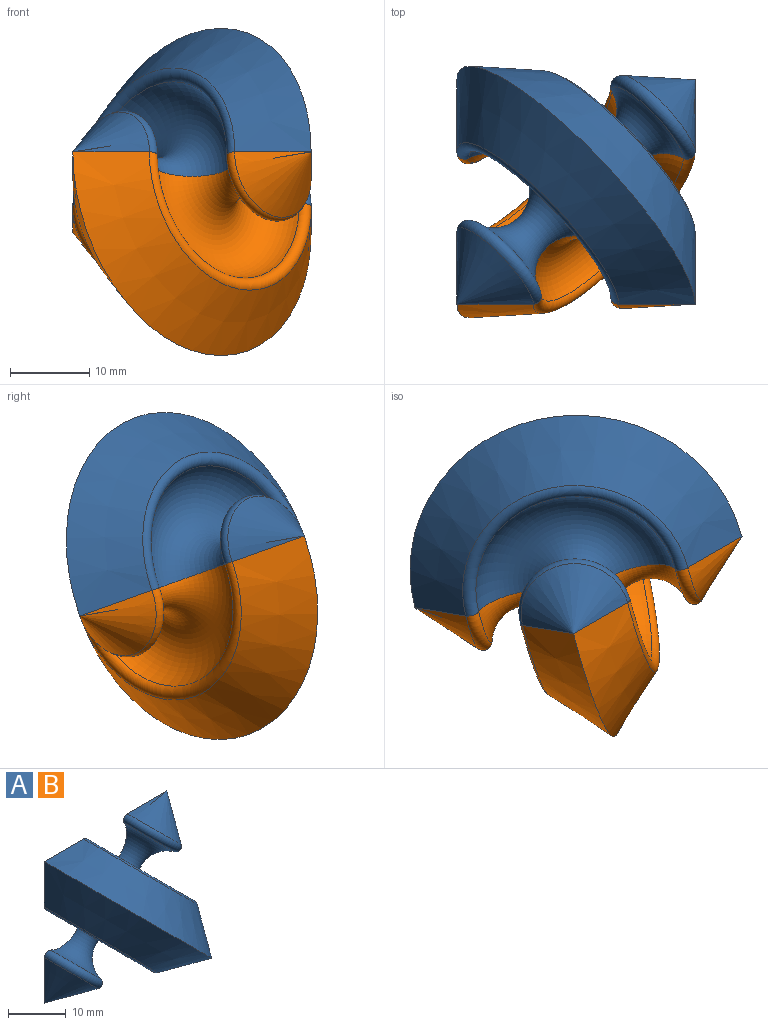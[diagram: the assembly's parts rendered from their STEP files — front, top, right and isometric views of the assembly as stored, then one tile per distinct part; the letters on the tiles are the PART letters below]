
ASSEMBLY  parts=2 mates=1
PART A: 11 faces, bbox 31.7x21.2x31.7 mm
  f0: torus R=7.78mm, axis (-0.71,0,-0.71), area 420.7mm2, adj f6,f7,f10
  f1: cone r=12.9mm half-angle=45deg, axis (-0.71,0,-0.71), area 538.8mm2, adj f2,f6,f7
  f2: cone r=21.21mm half-angle=45deg, axis (0.71,0,0.71), area 538.8mm2, adj f1,f6,f8
  f3: torus R=7.78mm, axis (-0.71,0,-0.71), area 420.7mm2, adj f6,f8,f9
  f4: cone r=8.31mm half-angle=45deg, axis (0.71,0,0.71), area 103mm2, adj f6,f9
  f5: cone r=0mm half-angle=45deg, axis (-0.71,0,-0.71), area 103mm2, adj f6,f10
  f6: plane 30x30mm, normal (0,1,0), area 580.2mm2, adj f0,f1,f2,f3,f4,f5,f7,f8
  f7: torus R=13.7mm, axis (0.71,0,0.71), area 88.1mm2, adj f0,f1,f6
  f8: torus R=13.7mm, axis (0.71,0,0.71), area 88.1mm2, adj f2,f3,f6
  f9: torus R=6.1mm, axis (0.71,0,0.71), area 45.1mm2, adj f3,f4,f6
  f10: torus R=6.1mm, axis (0.71,0,0.71), area 45.1mm2, adj f0,f5,f6
PART B: same geometry as A
PLACE A rot(axis=(-1,0,0),109.7deg) t=(2.34,3.81,-11.33)mm
PLACE B rot(axis=(1,0,0),70.3deg) t=(2.34,3.81,-11.33)mm
MATE revolute A.f6 <-> B.f6  axis (0,-0.34,-0.94) through (2.34,3.81,-11.33)mm
